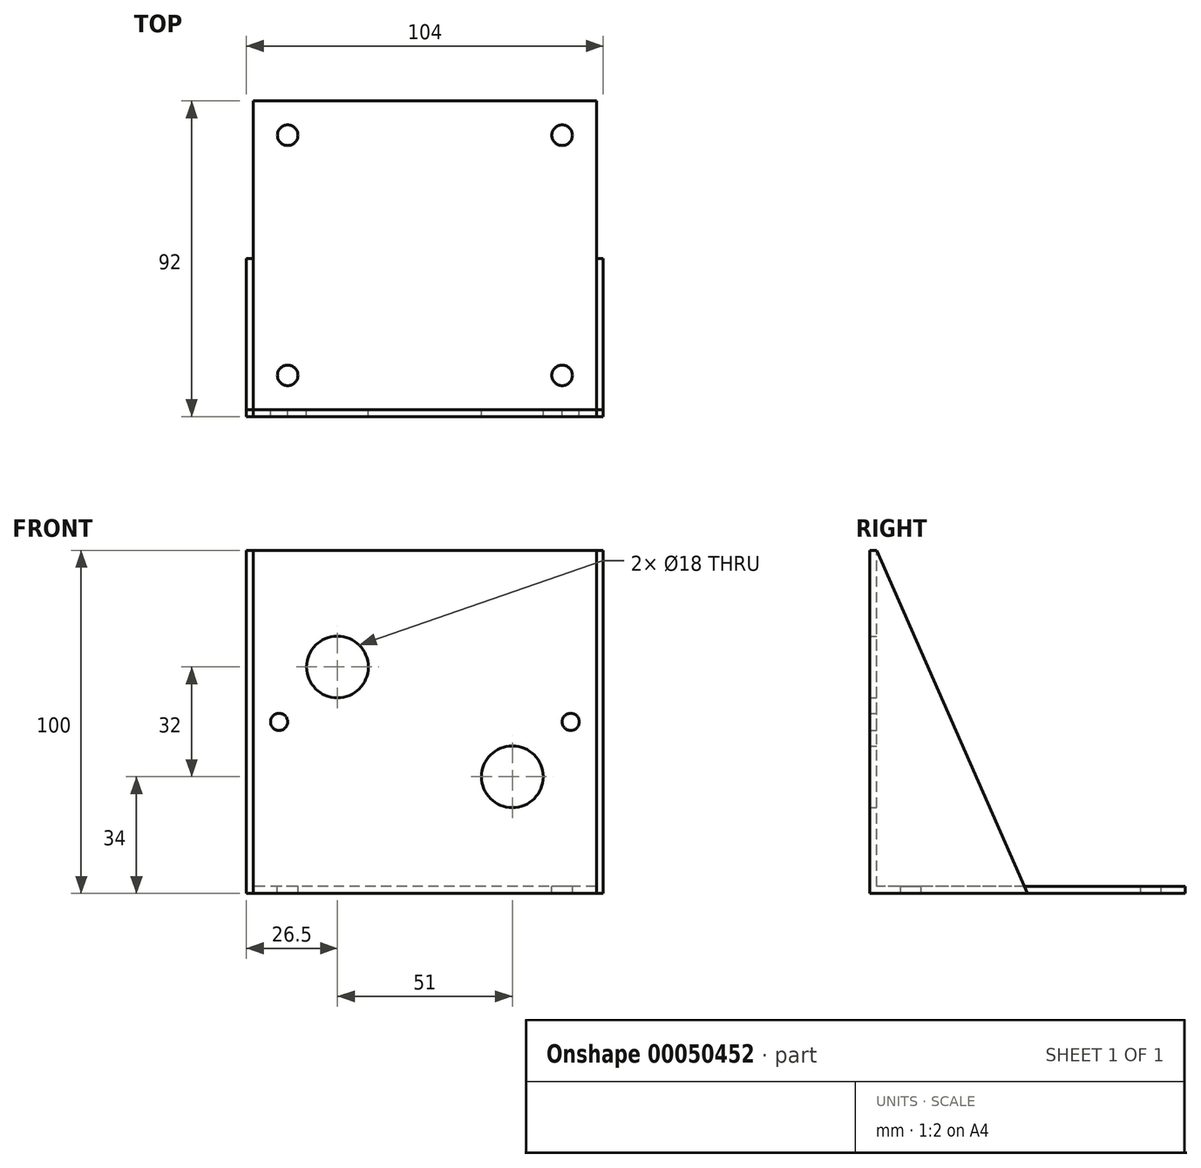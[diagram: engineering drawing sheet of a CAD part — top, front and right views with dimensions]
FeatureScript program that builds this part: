
annotation { "Feature Type Name" : "Feature", "Feature Type Description" : "" }
export const myFeature = defineFeature(function(context is Context, id is Id, definition is map)
    precondition{}
    {
        {
            var Q0;
            Q0=qCreatedBy(makeId("Front.planeOp"),FACE);
            var sketch = newSketch(context, id + "F0", { "sketchPlane" : qUnion([Q0])});
            skLineSegment(sketch, "E0.rect.bottom", {"start": v(50, -50) * mm, "end": v(-50, -50) * mm});
            skLineSegment(sketch, "E0.rect.top", {"start": v(50, 50) * mm, "end": v(-50, 50) * mm});
            skLineSegment(sketch, "E0.rect.left", {"start": v(50, -50) * mm, "end": v(50, 50) * mm});
            skLineSegment(sketch, "E0.rect.right", {"start": v(-50, -50) * mm, "end": v(-50, 50) * mm});
            skPoint(sketch, "E0.rect.middle", {"position": v(0, 0) * mm});
            skCircle(sketch, "E1", {"center": v(-42.5, 0) * mm, "radius": 2.5 * mm});
            skPoint(sketch, "E1.centerSnap0", {"position": v(-50, 0) * mm});
            skCircle(sketch, "E2", {"center": v(42.5, 0) * mm, "radius": 2.5 * mm});
            skCircle(sketch, "E3", {"center": v(25.5, -16) * mm, "radius": 9 * mm});
            skCircle(sketch, "E4.MirrorC", {"center": v(-25.5, 16) * mm, "radius": 9 * mm});
            skSolve(sketch);
        }
        {
            var Q0;
            Q0 = qSketchRegion(id + "F0", true);
            extrude(context, id + "F1", {"entities" : qUnion([Q0]), "depth" : 2 * mm});
        }
        {
            var Q0;
            Q0=makeQuery(id+"F1.opExtrude","CAP_FACE",FACE,{"disambiguationData":[OSD([sQuery(id+"F0.wireOp",EDGE,"E0.rect.bottom"),sQuery(id+"F0.wireOp",EDGE,"E0.rect.top"),sQuery(id+"F0.wireOp",EDGE,"E0.rect.left"),sQuery(id+"F0.wireOp",EDGE,"E0.rect.right"),sQuery(id+"F0.wireOp",EDGE,"E1"),sQuery(id+"F0.wireOp",EDGE,"E2"),sQuery(id+"F0.wireOp",EDGE,"E3")])],"isStart":true});
            var sketch = newSketch(context, id + "F2", { "sketchPlane" : qUnion([Q0])});
            skLineSegment(sketch, "E5.bottom", {"start": v(-50, -50) * mm, "end": v(50, -50) * mm});
            skLineSegment(sketch, "E5.top", {"start": v(-50, -48) * mm, "end": v(50, -48) * mm});
            skLineSegment(sketch, "E5.left", {"start": v(-50, -50) * mm, "end": v(-50, -48) * mm});
            skLineSegment(sketch, "E5.right", {"start": v(50, -50) * mm, "end": v(50, -48) * mm});
            skSolve(sketch);
        }
        {
            var Q0;
            Q0 = qSketchRegion(id + "F2", true);
            extrude(context, id + "F3", {"entities" : qUnion([Q0]), "operationType" : NewBodyOperationType.ADD, "depth" : 90 * mm});
        }
        {
            var Q0;
            Q0=makeQuery(id+"F3.opExtrude","SWEPT_FACE",FACE,{"disambiguationData":[OSD([sQuery(id+"F2.wireOp",EDGE,"E5.top")])]});
            var sketch = newSketch(context, id + "F4", { "sketchPlane" : qUnion([Q0])});
            skCircle(sketch, "E6", {"center": v(-40, 80) * mm, "radius": 3 * mm});
            skLineSegment(sketch, "E7", {"start": v(0, 90) * mm, "end": v(0, 0) * mm, "construction": true});
            skLineSegment(sketch, "E8", {"start": v(-50, 45) * mm, "end": v(50, 45) * mm, "construction": true});
            skCircle(sketch, "E9.MirrorC", {"center": v(40, 80) * mm, "radius": 3 * mm});
            skLineSegment(sketch, "E10.MirrorCS", {"start": v(50, 45) * mm, "end": v(-50, 45) * mm, "construction": true});
            skCircle(sketch, "E11.MirrorC", {"center": v(-40, 10) * mm, "radius": 3 * mm});
            skCircle(sketch, "E12.MirrorC", {"center": v(40, 10) * mm, "radius": 3 * mm});
            skLineSegment(sketch, "E13.MirrorCS", {"start": v(0, 0) * mm, "end": v(0, 90) * mm, "construction": true});
            skSolve(sketch);
        }
        {
            var Q0;
            Q0 = qSketchRegion(id + "F4", true);
            extrude(context, id + "F5", {"entities" : qUnion([Q0]), "operationType" : NewBodyOperationType.REMOVE, "oppositeDirection" : true, "depth" : 25 * mm});
        }
        {
            var Q0;
            Q0=makeQuery(id+"F3.boolean.opBoolean","MERGE",FACE,{"derivedFrom":[makeQuery(id+"F1.opExtrude","SWEPT_FACE",FACE,{"disambiguationData":[OSD([sQuery(id+"F0.wireOp",EDGE,"E0.rect.left")])]}),makeQuery(id+"F3.opExtrude","SWEPT_FACE",FACE,{"disambiguationData":[OSD([sQuery(id+"F2.wireOp",EDGE,"E5.left")])]})]});
            var sketch = newSketch(context, id + "F6", { "sketchPlane" : qUnion([Q0])});
            skLineSegment(sketch, "E14", {"start": v(-2, 50) * mm, "end": v(-2, -50) * mm});
            skLineSegment(sketch, "E15", {"start": v(-2, -50) * mm, "end": v(44, -50) * mm});
            skLineSegment(sketch, "E16", {"start": v(-2, 50) * mm, "end": v(0, 50) * mm});
            skLineSegment(sketch, "E17", {"start": v(0, 50) * mm, "end": v(44, -50) * mm});
            skSolve(sketch);
        }
        {
            var Q0;
            Q0 = qSketchRegion(id + "F6", true);
            extrude(context, id + "F7", {"entities" : qUnion([Q0]), "depth" : 2 * mm});
        }
        {
            var Q0;
            Q0=makeQuery(id+"F7.opExtrude","SWEPT_BODY",BODY,{"disambiguationData":[OSD([sQuery(id+"F6.wireOp",EDGE,"E14"),sQuery(id+"F6.wireOp",EDGE,"E15"),sQuery(id+"F6.wireOp",EDGE,"E16"),sQuery(id+"F6.wireOp",EDGE,"E17")])]});
            var Q1;
            Q1=qCreatedBy(makeId("Right.planeOp"),FACE);
            mirror(context, id + "F8", {"entities" : qUnion([Q0]), "mirrorPlane" : qUnion([Q1])});
        }
    });
